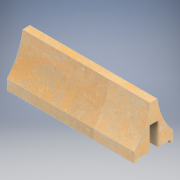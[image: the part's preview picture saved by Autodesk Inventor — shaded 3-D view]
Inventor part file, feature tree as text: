
AUTODESK INVENTOR PART (.ipt)
format: ipt  version: 2022.2 (Build 262287010, 287A)  size: 171,520 bytes
history: native  units: in
note: dims shown in document units (in); Inventor stores cm internally (conversion verified against a paired STEP export)
features: revolve x2, other x1, direct_edit x1
ambient origin geometry x8: Origin, YZ Plane, XZ Plane, XY Plane, X Axis, Y Axis, Z Axis, Center Point
bodies: Solid1 (feature_tree)
feature tree (4):
  other  "Mull (3)"
  direct_edit  "Direct Edit1"
  revolve  "Rotate1"  Angle=90.0deg
  revolve  "Rotate2"  Angle=180.0deg
